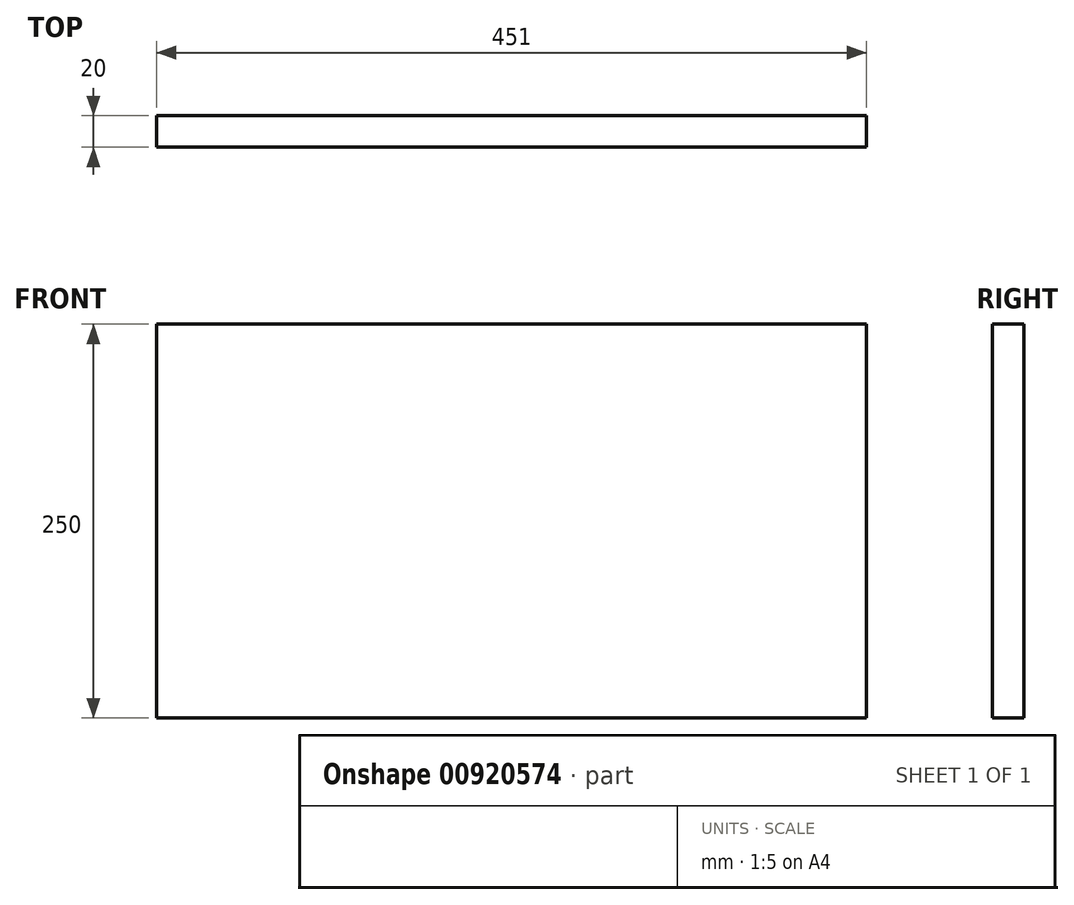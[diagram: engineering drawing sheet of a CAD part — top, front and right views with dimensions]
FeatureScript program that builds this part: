
annotation { "Feature Type Name" : "Feature", "Feature Type Description" : "" }
export const myFeature = defineFeature(function(context is Context, id is Id, definition is map)
    precondition{}
    {
        {
            var Q0;
            Q0=qCreatedBy(makeId("Front.planeOp"),FACE);
            var sketch = newSketch(context, id + "F0", { "sketchPlane" : qUnion([Q0])});
            skLineSegment(sketch, "E0.bottom", {"start": v(225.5, -125) * mm, "end": v(-225.5, -125) * mm});
            skLineSegment(sketch, "E0.top", {"start": v(225.5, 125) * mm, "end": v(-225.5, 125) * mm});
            skLineSegment(sketch, "E0.left", {"start": v(225.5, -125) * mm, "end": v(225.5, 125) * mm});
            skLineSegment(sketch, "E0.right", {"start": v(-225.5, -125) * mm, "end": v(-225.5, 125) * mm});
            skPoint(sketch, "E0.middle", {"position": v(0, 0) * mm});
            skSolve(sketch);
        }
        {
            var Q0;
            Q0=qSketchRegion(id+"F0",true);
            extrude(context, id + "F1", {"entities" : qUnion([Q0]), "depth" : 20 * mm, "symmetric" : true});
        }
    });
